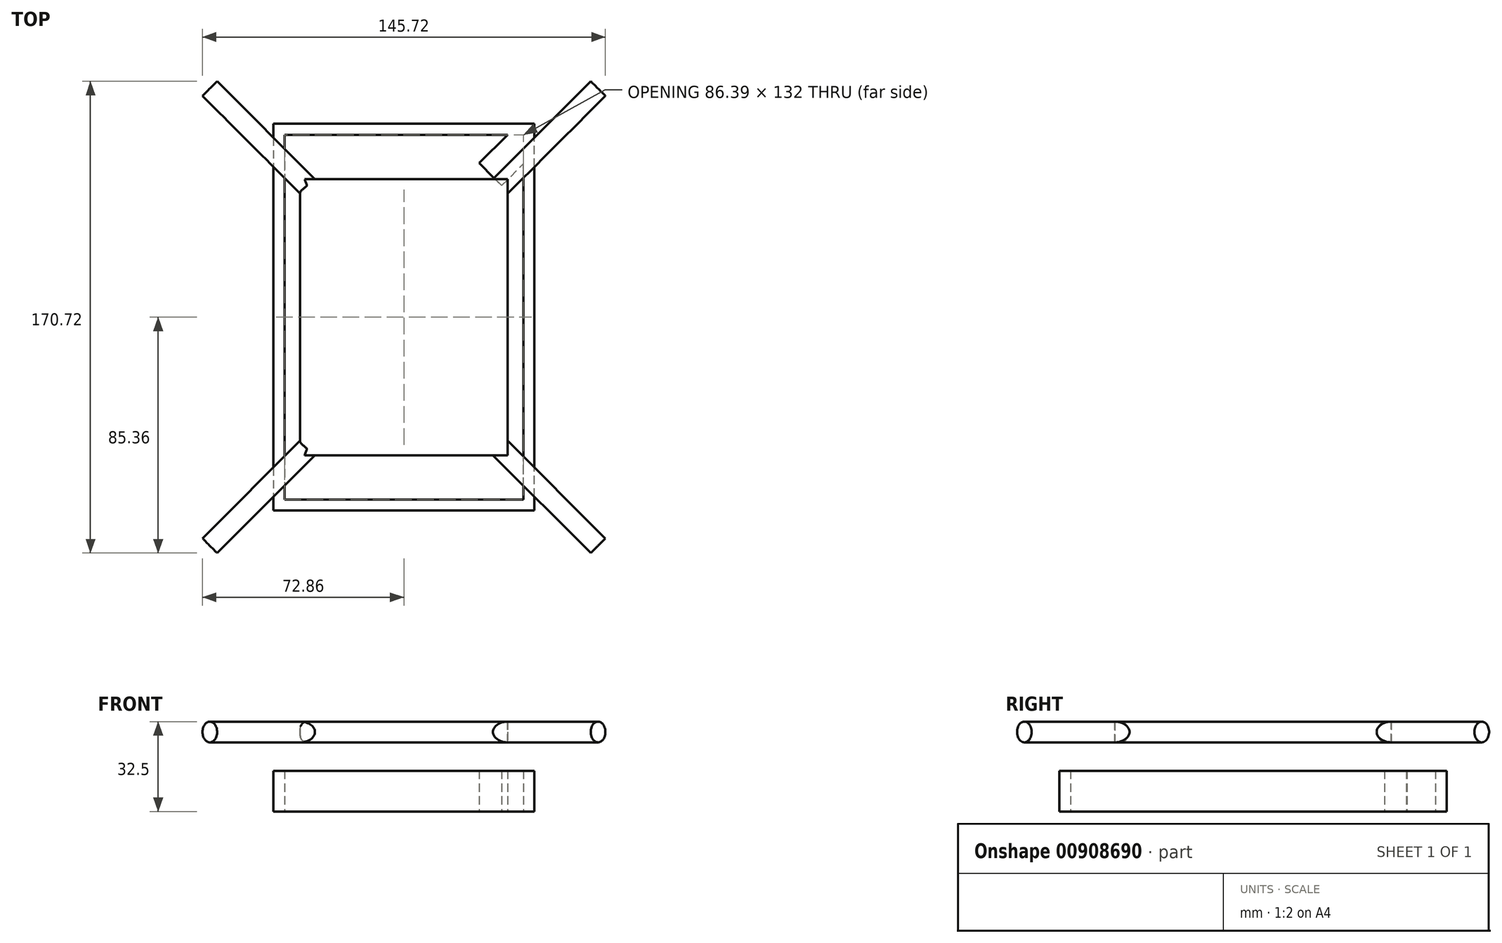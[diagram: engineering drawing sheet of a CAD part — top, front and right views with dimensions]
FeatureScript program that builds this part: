
annotation { "Feature Type Name" : "Feature", "Feature Type Description" : "" }
export const myFeature = defineFeature(function(context is Context, id is Id, definition is map)
    precondition{}
    {
        {
            assignVariable(context, id + "F0", {"name" : "LegDiameter", "anyValue" : 7.5});
        }
        {
            assignVariable(context, id + "F1", {"name" : "LegHeight", "anyValue" : 25});
        }
        {
            var Q0;
            Q0=qCreatedBy(makeId("Top.planeOp"),FACE);
            cPlane(context, id + "F2", {"entities" : qUnion([Q0]), "cplaneType" : CPlaneType.OFFSET, "offset" : (getVariable(context, 'LegHeight')) * mm, "width" : 150 * mm, "height" : 150 * mm});
        }
        {
            var Q0;
            Q0=qCreatedBy(id+"F2.planeOp",FACE);
            var sketch = newSketch(context, id + "F3", { "sketchPlane" : qUnion([Q0])});
            skLineSegment(sketch, "E0", {"start": v(37.5, 0) * mm, "end": v(37.5, 44.7) * mm});
            skLineSegment(sketch, "E1", {"start": v(37.5, 44.7) * mm, "end": v(72.86, 80.05) * mm});
            skLineSegment(sketch, "E2", {"start": v(72.86, 80.05) * mm, "end": v(67.55, 85.36) * mm});
            skLineSegment(sketch, "E3", {"start": v(67.55, 85.36) * mm, "end": v(32.2, 50) * mm});
            skLineSegment(sketch, "E4", {"start": v(32.2, 50) * mm, "end": v(0, 50) * mm});
            skLineSegment(sketch, "E5", {"start": v(0, 50) * mm, "end": v(0, 0) * mm, "construction": true});
            skLineSegment(sketch, "E6", {"start": v(0, 0) * mm, "end": v(37.5, 0) * mm, "construction": true});
            skLineSegment(sketch, "E7.MirrorCS", {"start": v(-72.86, 80.05) * mm, "end": v(-67.55, 85.36) * mm});
            skLineSegment(sketch, "E8.MirrorCS", {"start": v(-32.2, 50) * mm, "end": v(0, 50) * mm});
            skLineSegment(sketch, "E9.MirrorCS", {"start": v(-37.5, 0) * mm, "end": v(-37.5, 44.7) * mm});
            skLineSegment(sketch, "E10.MirrorCS", {"start": v(0, 0) * mm, "end": v(-37.5, 0) * mm, "construction": true});
            skLineSegment(sketch, "E11.MirrorCS", {"start": v(-37.5, 44.7) * mm, "end": v(-72.86, 80.05) * mm});
            skLineSegment(sketch, "E12.MirrorCS", {"start": v(-67.55, 85.36) * mm, "end": v(-32.2, 50) * mm});
            skLineSegment(sketch, "E13.MirrorCS", {"start": v(-37.5, 0) * mm, "end": v(-37.5, -44.7) * mm});
            skLineSegment(sketch, "E14.MirrorCS", {"start": v(-72.86, -80.05) * mm, "end": v(-67.55, -85.36) * mm});
            skLineSegment(sketch, "E15.MirrorCS", {"start": v(72.86, -80.05) * mm, "end": v(67.55, -85.36) * mm});
            skLineSegment(sketch, "E16.MirrorCS", {"start": v(37.5, -44.7) * mm, "end": v(72.86, -80.05) * mm});
            skLineSegment(sketch, "E17.MirrorCS", {"start": v(-32.2, -50) * mm, "end": v(0, -50) * mm});
            skLineSegment(sketch, "E18.MirrorCS", {"start": v(37.5, 0) * mm, "end": v(37.5, -44.7) * mm});
            skLineSegment(sketch, "E19.MirrorCS", {"start": v(67.55, -85.36) * mm, "end": v(32.2, -50) * mm});
            skLineSegment(sketch, "E20.MirrorCS", {"start": v(32.2, -50) * mm, "end": v(0, -50) * mm});
            skLineSegment(sketch, "E21.MirrorCS", {"start": v(-37.5, -44.7) * mm, "end": v(-72.86, -80.05) * mm});
            skLineSegment(sketch, "E22.MirrorCS", {"start": v(0, -50) * mm, "end": v(0, 0) * mm, "construction": true});
            skLineSegment(sketch, "E23.MirrorCS", {"start": v(-67.55, -85.36) * mm, "end": v(-32.2, -50) * mm});
            skSolve(sketch);
        }
        {
            var Q0;
            Q0 = qSketchRegion(id + "F3", true);
            extrude(context, id + "F4", {"entities" : qUnion([Q0]), "depth" : (getVariable(context, 'LegDiameter')) * mm, "offsetDistance" : 25 * mm});
        }
        {
            var Q0;
            Q0=makeQuery(id+"F4.opExtrude","CAP_EDGE",EDGE,{"disambiguationData":[OSD([sQuery(id+"F3.wireOp",EDGE,"E11.MirrorCS")])],"isStart":false});
            var Q1;
            Q1=makeQuery(id+"F4.opExtrude","CAP_EDGE",EDGE,{"disambiguationData":[OSD([sQuery(id+"F3.wireOp",EDGE,"E11.MirrorCS")])],"isStart":true});
            var Q2;
            Q2=makeQuery(id+"F4.opExtrude","CAP_EDGE",EDGE,{"disambiguationData":[OSD([sQuery(id+"F3.wireOp",EDGE,"E12.MirrorCS")])],"isStart":false});
            var Q3;
            Q3=makeQuery(id+"F4.opExtrude","CAP_EDGE",EDGE,{"disambiguationData":[OSD([sQuery(id+"F3.wireOp",EDGE,"E12.MirrorCS")])],"isStart":true});
            var Q4;
            Q4=makeQuery(id+"F4.opExtrude","CAP_EDGE",EDGE,{"disambiguationData":[OSD([sQuery(id+"F3.wireOp",EDGE,"E3")])],"isStart":true});
            var Q5;
            Q5=makeQuery(id+"F4.opExtrude","CAP_EDGE",EDGE,{"disambiguationData":[OSD([sQuery(id+"F3.wireOp",EDGE,"E1")])],"isStart":true});
            var Q6;
            Q6=makeQuery(id+"F4.opExtrude","CAP_EDGE",EDGE,{"disambiguationData":[OSD([sQuery(id+"F3.wireOp",EDGE,"E3")])],"isStart":false});
            var Q7;
            Q7=makeQuery(id+"F4.opExtrude","CAP_EDGE",EDGE,{"disambiguationData":[OSD([sQuery(id+"F3.wireOp",EDGE,"E16.MirrorCS")])],"isStart":false});
            var Q8;
            Q8=makeQuery(id+"F4.opExtrude","CAP_EDGE",EDGE,{"disambiguationData":[OSD([sQuery(id+"F3.wireOp",EDGE,"E16.MirrorCS")])],"isStart":true});
            var Q9;
            Q9=makeQuery(id+"F4.opExtrude","CAP_EDGE",EDGE,{"disambiguationData":[OSD([sQuery(id+"F3.wireOp",EDGE,"E19.MirrorCS")])],"isStart":true});
            var Q10;
            Q10=makeQuery(id+"F4.opExtrude","CAP_EDGE",EDGE,{"disambiguationData":[OSD([sQuery(id+"F3.wireOp",EDGE,"E23.MirrorCS")])],"isStart":true});
            var Q11;
            Q11=makeQuery(id+"F4.opExtrude","CAP_EDGE",EDGE,{"disambiguationData":[OSD([sQuery(id+"F3.wireOp",EDGE,"E21.MirrorCS")])],"isStart":true});
            var Q12;
            Q12=makeQuery(id+"F4.opExtrude","CAP_EDGE",EDGE,{"disambiguationData":[OSD([sQuery(id+"F3.wireOp",EDGE,"E21.MirrorCS")])],"isStart":false});
            var Q13;
            Q13=makeQuery(id+"F4.opExtrude","CAP_EDGE",EDGE,{"disambiguationData":[OSD([sQuery(id+"F3.wireOp",EDGE,"E23.MirrorCS")])],"isStart":false});
            var Q14;
            Q14=makeQuery(id+"F4.opExtrude","CAP_EDGE",EDGE,{"disambiguationData":[OSD([sQuery(id+"F3.wireOp",EDGE,"E19.MirrorCS")])],"isStart":false});
            var Q15;
            Q15=makeQuery(id+"F4.opExtrude","CAP_EDGE",EDGE,{"disambiguationData":[OSD([sQuery(id+"F3.wireOp",EDGE,"E1")])],"isStart":false});
            fillet(context, id + "F5", {"entities" : qUnion([Q0, Q1, Q2, Q3, Q4, Q5, Q6, Q7, Q8, Q9, Q10, Q11, Q12, Q13, Q14, Q15]), "radius" : (getVariable(context, 'LegDiameter') / 2) * mm, "tangentPropagation" : true, "allowEdgeOverflow" : false});
        }
        {
            var Q0;
            Q0=makeQuery(id+"F4.opExtrude","CAP_EDGE",EDGE,{"disambiguationData":[OSD([sQuery(id+"F3.wireOp",EDGE,"E9.MirrorCS"),sQuery(id+"F3.wireOp",EDGE,"E13.MirrorCS")])],"isStart":false});
            var Q1;
            Q1=makeQuery(id+"F4.opExtrude","CAP_EDGE",EDGE,{"disambiguationData":[OSD([sQuery(id+"F3.wireOp",EDGE,"E9.MirrorCS"),sQuery(id+"F3.wireOp",EDGE,"E13.MirrorCS")])],"isStart":true});
            fillet(context, id + "F6", {"entities" : qUnion([Q0, Q1]), "radius" : 2.5 * mm, "tangentPropagation" : true, "allowEdgeOverflow" : false});
        }
        {
            var Q0;
            Q0=qCreatedBy(makeId("Top.planeOp"),FACE);
            var sketch = newSketch(context, id + "F7", { "sketchPlane" : qUnion([Q0])});
            skLineSegment(sketch, "E24", {"start": v(-47.2, 70) * mm, "end": v(-47.2, -70) * mm});
            skLineSegment(sketch, "E25", {"start": v(-47.2, -70) * mm, "end": v(47.2, -70) * mm});
            skLineSegment(sketch, "E26", {"start": v(47.2, -70) * mm, "end": v(47.2, 70) * mm});
            skLineSegment(sketch, "E27", {"start": v(47.2, 70) * mm, "end": v(-47.2, 70) * mm});
            skLineSegment(sketch, "E28", {"start": v(-67.55, 85.36) * mm, "end": v(-32.2, 50) * mm, "construction": true});
            skLineSegment(sketch, "E29", {"start": v(-32.2, -50) * mm, "end": v(-67.55, -85.36) * mm, "construction": true});
            skLineSegment(sketch, "E30", {"start": v(67.55, -85.36) * mm, "end": v(32.2, -50) * mm, "construction": true});
            skLineSegment(sketch, "E31", {"start": v(32.2, 50) * mm, "end": v(67.55, 85.36) * mm, "construction": true});
            skPoint(sketch, "E32", {"position": v(-47.2, 65) * mm});
            skPoint(sketch, "E33", {"position": v(47.2, 65) * mm});
            skPoint(sketch, "E34", {"position": v(47.2, -65) * mm});
            skPoint(sketch, "E35", {"position": v(-47.2, -65) * mm});
            skLineSegment(sketch, "E36.0", {"start": v(37.46, 66) * mm, "end": v(-43.2, 66) * mm});
            skLineSegment(sketch, "E36.1", {"start": v(43.2, -66) * mm, "end": v(43.2, 55.47) * mm});
            skLineSegment(sketch, "E36.2", {"start": v(-43.2, -66) * mm, "end": v(43.2, -66) * mm});
            skLineSegment(sketch, "E36.3", {"start": v(-43.2, 66) * mm, "end": v(-43.2, -66) * mm});
            skLineSegment(sketch, "E37", {"start": v(37.46, 66) * mm, "end": v(27.2, 55.75) * mm});
            skLineSegment(sketch, "E38", {"start": v(27.2, 55.75) * mm, "end": v(35.34, 47.61) * mm});
            skLineSegment(sketch, "E39", {"start": v(35.34, 47.61) * mm, "end": v(43.2, 55.47) * mm});
            skSolve(sketch);
        }
        {
            var Q0;
            Q0 = qSketchRegion(id + "F7", true);
            extrude(context, id + "F8", {"entities" : qUnion([Q0]), "depth" : 14.7 * mm, "offsetDistance" : 25 * mm});
        }
    });
